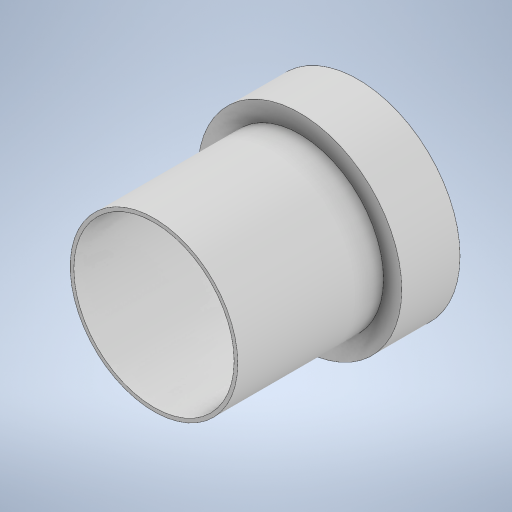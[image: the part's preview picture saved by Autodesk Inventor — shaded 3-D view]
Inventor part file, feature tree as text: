
AUTODESK INVENTOR PART (.ipt)
format: ipt  version: 2024.2 (Build 282272000, 272)  size: 240,640 bytes
history: native  units: mm
features: extrude x2, sketch x1
ambient origin geometry x8: Origin, YZ Plane, XZ Plane, XY Plane, X Axis, Y Axis, Z Axis, Center Point
bodies: Solid1 (feature_tree)
feature tree (3):
  extrude  "Extrusion1"  Depth=4.0mm
  extrude  "Extrusion2"  Depth=10.0mm TaperAngle=0.0deg
  sketch  "Sketch2"  dims[d0=11.0mm d1=11.5mm d2=10.0mm d3=0.0mm d4=14.0mm d5=4.0mm d6=0.0mm]
